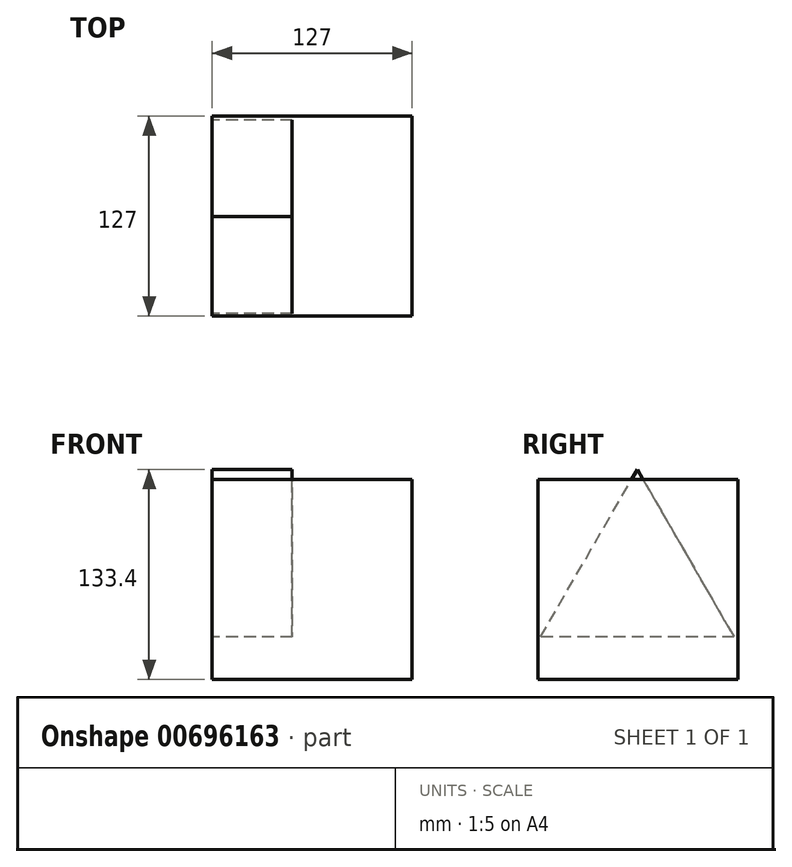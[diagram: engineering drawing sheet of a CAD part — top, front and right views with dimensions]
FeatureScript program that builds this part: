
annotation { "Feature Type Name" : "Feature", "Feature Type Description" : "" }
export const myFeature = defineFeature(function(context is Context, id is Id, definition is map)
    precondition{}
    {
        {
            var Q0;
            Q0=qCreatedBy(makeId("Right.planeOp"),FACE);
            var sketch = newSketch(context, id + "F0", { "sketchPlane" : qUnion([Q0])});
            skCircle(sketch, "E0.cCircle", {"center": v(0, 0) * mm, "radius": 35.5 * mm, "construction": true});
            skLineSegment(sketch, "E0.0", {"start": v(-61.5, -35.5) * mm, "end": v(0, 71) * mm});
            skLineSegment(sketch, "E0.1", {"start": v(0, 71) * mm, "end": v(61.5, -35.5) * mm});
            skLineSegment(sketch, "E0.2", {"start": v(61.5, -35.5) * mm, "end": v(-61.5, -35.5) * mm});
            skPoint(sketch, "E0.0.midPoint", {"position": v(-30.75, 17.75) * mm});
            skSolve(sketch);
        }
        {
            var Q0;
            Q0=qCreatedBy(makeId("Right.planeOp"),FACE);
            var sketch = newSketch(context, id + "F1", { "sketchPlane" : qUnion([Q0])});
            skLineSegment(sketch, "E1", {"start": v(-63.01, 64.61) * mm, "end": v(-63.01, -62.39) * mm});
            skLineSegment(sketch, "E2", {"start": v(-63.01, -62.39) * mm, "end": v(63.99, -62.39) * mm});
            skLineSegment(sketch, "E3", {"start": v(63.99, -62.39) * mm, "end": v(63.99, 64.61) * mm});
            skLineSegment(sketch, "E4", {"start": v(-63.01, 64.61) * mm, "end": v(63.99, 64.61) * mm});
            skSolve(sketch);
        }
        {
            var Q0;
            Q0=makeQuery(id+"F1.imprint","IMPRINT",FACE,{"disambiguationData":[TD([[makeQuery(id+"F1.imprint","IMPRINT",EDGE,{"derivedFrom":sQuery(id+"F1.wireOp",EDGE,"E1")}),1.0]])]});
            extrude(context, id + "F2", {"entities" : qUnion([Q0]), "depth" : 127 * mm, "offsetDistance" : 25.4 * mm});
        }
        {
            var Q0;
            Q0 = qSketchRegion(id + "F0", true);
            extrude(context, id + "F3", {"entities" : qUnion([Q0]), "depth" : 50.8 * mm, "offsetDistance" : 25.4 * mm});
        }
    });
